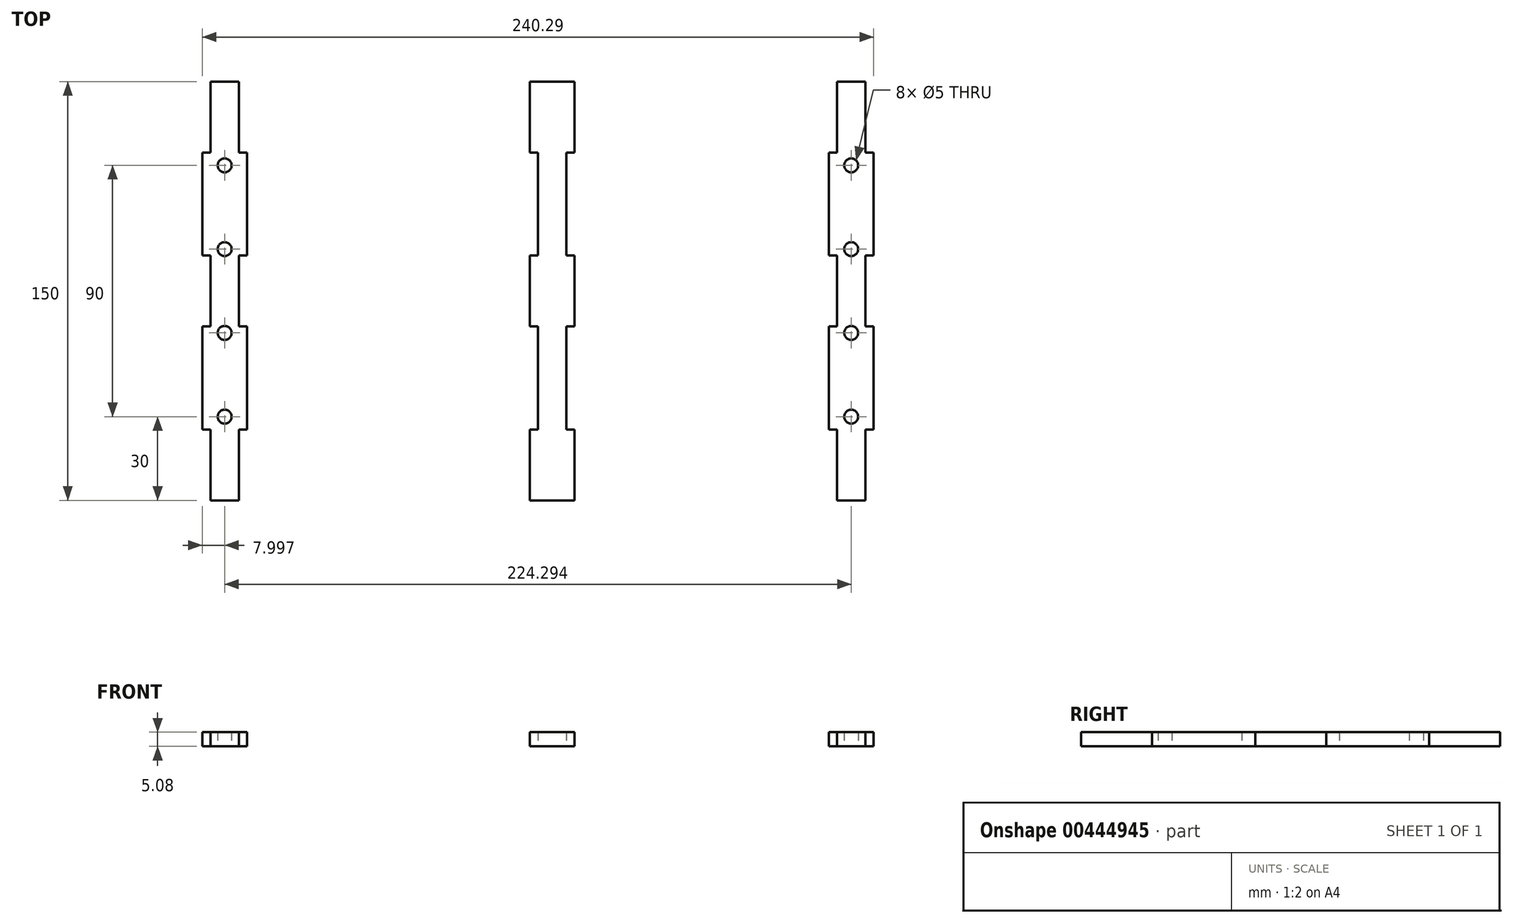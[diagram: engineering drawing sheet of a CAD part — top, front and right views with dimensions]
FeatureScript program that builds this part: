
annotation { "Feature Type Name" : "Feature", "Feature Type Description" : "" }
export const myFeature = defineFeature(function(context is Context, id is Id, definition is map)
    precondition{}
    {
        {
            var Q0;
            Q0=qCreatedBy(makeId("Top.planeOp"),FACE);
            var sketch = newSketch(context, id + "F0", { "sketchPlane" : qUnion([Q0])});
            skLineSegment(sketch, "E0", {"start": v(0, 124.6) * mm, "end": v(0, 87.7) * mm});
            skLineSegment(sketch, "E1", {"start": v(-10.16, 124.6) * mm, "end": v(-10.16, 87.7) * mm});
            skLineSegment(sketch, "E2", {"start": v(-10.16, 150) * mm, "end": v(0, 150) * mm});
            skLineSegment(sketch, "E3", {"start": v(-10.16, 0) * mm, "end": v(0, 0) * mm});
            skLineSegment(sketch, "E4", {"start": v(0, 150) * mm, "end": v(2.92, 150) * mm});
            skLineSegment(sketch, "E5", {"start": v(2.92, 124.6) * mm, "end": v(0, 124.6) * mm});
            skLineSegment(sketch, "E6", {"start": v(0, 0) * mm, "end": v(2.92, 0) * mm});
            skLineSegment(sketch, "E7", {"start": v(2.92, 0) * mm, "end": v(2.92, 25.4) * mm});
            skLineSegment(sketch, "E8", {"start": v(2.92, 25.4) * mm, "end": v(0, 25.4) * mm});
            skLineSegment(sketch, "E9", {"start": v(-10.16, 150) * mm, "end": v(-13.08, 150) * mm});
            skLineSegment(sketch, "E10", {"start": v(-13.08, 150) * mm, "end": v(-13.08, 124.6) * mm});
            skLineSegment(sketch, "E11", {"start": v(-13.08, 124.6) * mm, "end": v(-10.16, 124.6) * mm});
            skPoint(sketch, "E12", {"position": v(-10.16, 62.3) * mm});
            skLineSegment(sketch, "E13", {"start": v(0, 62.3) * mm, "end": v(2.92, 62.3) * mm});
            skLineSegment(sketch, "E14", {"start": v(2.92, 62.3) * mm, "end": v(2.92, 87.7) * mm});
            skLineSegment(sketch, "E15", {"start": v(2.92, 87.7) * mm, "end": v(0, 87.7) * mm});
            skLineSegment(sketch, "E16.bottom", {"start": v(96.9, 0) * mm, "end": v(107.05, 0) * mm});
            skLineSegment(sketch, "E16.top", {"start": v(96.9, 150) * mm, "end": v(107.05, 150) * mm});
            skLineSegment(sketch, "E16.left", {"start": v(96.9, 0) * mm, "end": v(96.9, 25.4) * mm});
            skLineSegment(sketch, "E16.right", {"start": v(107.05, 0) * mm, "end": v(107.05, 25.4) * mm});
            skLineSegment(sketch, "E17", {"start": v(96.9, 124.6) * mm, "end": v(93.97, 124.6) * mm});
            skLineSegment(sketch, "E18", {"start": v(93.97, 124.6) * mm, "end": v(93.97, 87.7) * mm});
            skLineSegment(sketch, "E19", {"start": v(93.97, 87.7) * mm, "end": v(96.9, 87.7) * mm});
            skLineSegment(sketch, "E20", {"start": v(96.9, 62.3) * mm, "end": v(93.97, 62.3) * mm});
            skLineSegment(sketch, "E21", {"start": v(93.97, 62.3) * mm, "end": v(93.97, 25.4) * mm});
            skLineSegment(sketch, "E22", {"start": v(93.97, 25.4) * mm, "end": v(96.9, 25.4) * mm});
            skLineSegment(sketch, "E23", {"start": v(107.05, 124.6) * mm, "end": v(109.97, 124.6) * mm});
            skLineSegment(sketch, "E24", {"start": v(109.97, 124.6) * mm, "end": v(109.97, 87.7) * mm});
            skLineSegment(sketch, "E25", {"start": v(109.97, 87.7) * mm, "end": v(107.05, 87.7) * mm});
            skLineSegment(sketch, "E26", {"start": v(107.05, 62.3) * mm, "end": v(109.97, 62.3) * mm});
            skLineSegment(sketch, "E27", {"start": v(109.97, 62.3) * mm, "end": v(109.97, 25.4) * mm});
            skLineSegment(sketch, "E28", {"start": v(109.97, 25.4) * mm, "end": v(107.05, 25.4) * mm});
            skLineSegment(sketch, "E29.bottom", {"start": v(-127.4, 0) * mm, "end": v(-117.24, 0) * mm});
            skLineSegment(sketch, "E29.top", {"start": v(-127.4, 150) * mm, "end": v(-117.24, 150) * mm});
            skLineSegment(sketch, "E29.left", {"start": v(-127.4, 0) * mm, "end": v(-127.4, 25.4) * mm});
            skLineSegment(sketch, "E29.right", {"start": v(-117.24, 0) * mm, "end": v(-117.24, 25.4) * mm});
            skLineSegment(sketch, "E30", {"start": v(-117.24, 124.6) * mm, "end": v(-114.32, 124.6) * mm});
            skLineSegment(sketch, "E31", {"start": v(-114.32, 124.6) * mm, "end": v(-114.32, 87.7) * mm});
            skLineSegment(sketch, "E32", {"start": v(-114.32, 87.7) * mm, "end": v(-117.24, 87.7) * mm});
            skLineSegment(sketch, "E33", {"start": v(-117.24, 62.3) * mm, "end": v(-114.32, 62.3) * mm});
            skLineSegment(sketch, "E34", {"start": v(-114.32, 62.3) * mm, "end": v(-114.32, 25.4) * mm});
            skLineSegment(sketch, "E35", {"start": v(-114.32, 25.4) * mm, "end": v(-117.24, 25.4) * mm});
            skPoint(sketch, "E36.start.orphan", {"position": v(-127.4, 124.6) * mm});
            skPoint(sketch, "E37.end.orphan", {"position": v(-127.4, 87.7) * mm});
            skPoint(sketch, "E38.start.orphan", {"position": v(-127.4, 62.3) * mm});
            skPoint(sketch, "E39.end.orphan", {"position": v(-127.4, 25.4) * mm});
            skLineSegment(sketch, "E40", {"start": v(-127.4, 124.6) * mm, "end": v(-130.32, 124.6) * mm});
            skLineSegment(sketch, "E41", {"start": v(-130.32, 124.6) * mm, "end": v(-130.32, 87.7) * mm});
            skLineSegment(sketch, "E42", {"start": v(-130.32, 87.7) * mm, "end": v(-127.4, 87.7) * mm});
            skLineSegment(sketch, "E43", {"start": v(-127.4, 62.3) * mm, "end": v(-130.32, 62.3) * mm});
            skLineSegment(sketch, "E44", {"start": v(-130.32, 62.3) * mm, "end": v(-130.32, 25.4) * mm});
            skLineSegment(sketch, "E45", {"start": v(-130.32, 25.4) * mm, "end": v(-127.4, 25.4) * mm});
            skPoint(sketch, "E46.end.orphan", {"position": v(-10.16, 87.7) * mm});
            skPoint(sketch, "E47.start.orphan", {"position": v(-10.16, 25.4) * mm});
            skLineSegment(sketch, "E48", {"start": v(-10.16, 87.7) * mm, "end": v(-13.08, 87.7) * mm});
            skLineSegment(sketch, "E49", {"start": v(-13.08, 87.7) * mm, "end": v(-13.08, 62.3) * mm});
            skLineSegment(sketch, "E50", {"start": v(-13.08, 62.3) * mm, "end": v(-10.16, 62.3) * mm});
            skLineSegment(sketch, "E51", {"start": v(-10.16, 25.4) * mm, "end": v(-13.08, 25.4) * mm});
            skLineSegment(sketch, "E52", {"start": v(-13.08, 25.4) * mm, "end": v(-13.08, 0) * mm});
            skPoint(sketch, "E52.endSnap0", {"position": v(-5.08, 0) * mm});
            skLineSegment(sketch, "E53", {"start": v(-13.08, 0) * mm, "end": v(-10.16, 0) * mm});
            skLineSegment(sketch, "E54.trimOffspring", {"start": v(-10.16, 62.3) * mm, "end": v(-10.16, 25.4) * mm});
            skLineSegment(sketch, "E55.trimOffspring", {"start": v(0, 62.3) * mm, "end": v(0, 25.4) * mm});
            skLineSegment(sketch, "E56.trimOffspring", {"start": v(96.9, 62.3) * mm, "end": v(96.9, 87.7) * mm});
            skLineSegment(sketch, "E57.trimOffspring", {"start": v(107.05, 62.3) * mm, "end": v(107.05, 87.7) * mm});
            skLineSegment(sketch, "E58.trimOffspring", {"start": v(96.9, 124.6) * mm, "end": v(96.9, 150) * mm});
            skLineSegment(sketch, "E59.trimOffspring", {"start": v(107.05, 124.6) * mm, "end": v(107.05, 150) * mm});
            skLineSegment(sketch, "E60.trimOffspring", {"start": v(-117.24, 124.6) * mm, "end": v(-117.24, 150) * mm});
            skLineSegment(sketch, "E61.trimOffspring", {"start": v(-127.4, 124.6) * mm, "end": v(-127.4, 150) * mm});
            skLineSegment(sketch, "E62.trimOffspring", {"start": v(-127.4, 62.3) * mm, "end": v(-127.4, 87.7) * mm});
            skLineSegment(sketch, "E63.trimOffspring", {"start": v(-117.24, 62.3) * mm, "end": v(-117.24, 87.7) * mm});
            skLineSegment(sketch, "E64", {"start": v(2.92, 150) * mm, "end": v(2.92, 124.6) * mm});
            skPoint(sketch, "E65", {"position": v(-122.32, 120) * mm});
            skPoint(sketch, "E65.positionSnap0", {"position": v(-122.32, 150) * mm});
            skPoint(sketch, "E66", {"position": v(-122.32, 90) * mm});
            skPoint(sketch, "E67", {"position": v(-122.32, 60) * mm});
            skPoint(sketch, "E68", {"position": v(-122.32, 30) * mm});
            skPoint(sketch, "E69", {"position": v(101.97, 120) * mm});
            skPoint(sketch, "E69.positionSnap0", {"position": v(101.97, 150) * mm});
            skPoint(sketch, "E70", {"position": v(101.97, 90) * mm});
            skPoint(sketch, "E71", {"position": v(101.97, 60) * mm});
            skPoint(sketch, "E72", {"position": v(101.97, 30) * mm});
            skCircle(sketch, "E73", {"center": v(-122.32, 120) * mm, "radius": 2.5 * mm});
            skCircle(sketch, "E74", {"center": v(-122.32, 90) * mm, "radius": 2.5 * mm});
            skCircle(sketch, "E75", {"center": v(-122.32, 30) * mm, "radius": 2.5 * mm});
            skCircle(sketch, "E76", {"center": v(-122.32, 60) * mm, "radius": 2.5 * mm});
            skCircle(sketch, "E77", {"center": v(101.97, 120) * mm, "radius": 2.5 * mm});
            skCircle(sketch, "E78", {"center": v(101.97, 90) * mm, "radius": 2.5 * mm});
            skCircle(sketch, "E79", {"center": v(101.97, 60) * mm, "radius": 2.5 * mm});
            skCircle(sketch, "E80", {"center": v(101.97, 30) * mm, "radius": 2.5 * mm});
            skSolve(sketch);
        }
        {
            var Q0;
            Q0=makeQuery(id+"F0.imprint","IMPRINT",FACE,{"disambiguationData":[TD([[makeQuery(id+"F0.imprint","IMPRINT",EDGE,{"derivedFrom":sQuery(id+"F0.wireOp",EDGE,"E29.bottom")}),1.0]])]});
            var Q1;
            Q1=makeQuery(id+"F0.imprint","IMPRINT",FACE,{"disambiguationData":[TD([[makeQuery(id+"F0.imprint","IMPRINT",EDGE,{"derivedFrom":sQuery(id+"F0.wireOp",EDGE,"E0")}),-1.0]])]});
            var Q2;
            Q2=makeQuery(id+"F0.imprint","IMPRINT",FACE,{"disambiguationData":[TD([[makeQuery(id+"F0.imprint","IMPRINT",EDGE,{"derivedFrom":sQuery(id+"F0.wireOp",EDGE,"E16.bottom")}),1.0]])]});
            extrude(context, id + "F1", {"entities" : qUnion([Q0, Q1, Q2]), "depth" : 5.08 * mm});
        }
    });
